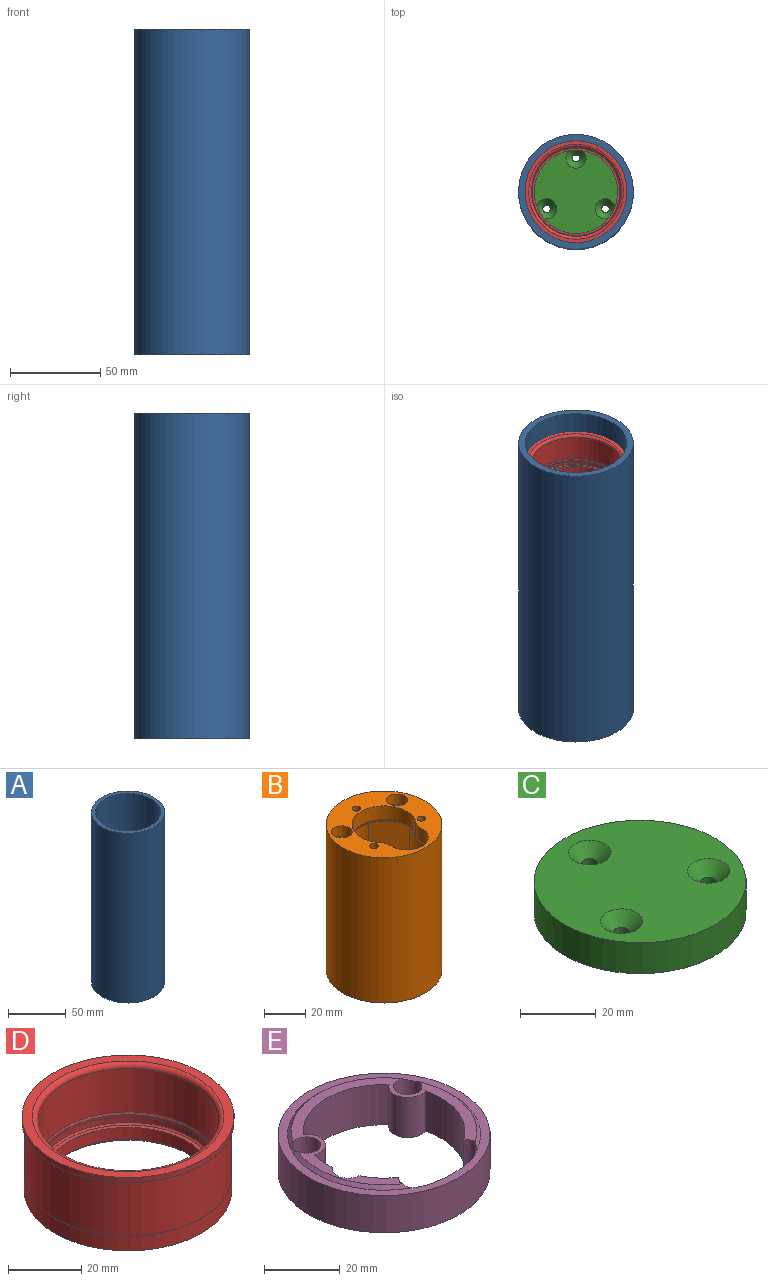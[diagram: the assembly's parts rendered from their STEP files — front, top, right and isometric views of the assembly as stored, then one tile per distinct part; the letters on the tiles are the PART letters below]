
ASSEMBLY  parts=5 mates=4
PART A: 8 faces, bbox 63.5x63.5x180 mm
  f0: cylinder r=31.75mm len=180mm, axis (0,0,-1), area 35908.4mm2, adj f2,f3
  f1: cylinder r=28.15mm len=167mm, axis (0,0,-1), area 29537.6mm2, adj f2,f5
  f2: plane 63.5x63.5mm, normal (0,0,1), area 677.5mm2, adj f0,f1
  f3: plane 63.5x63.5mm, normal (0,0,-1), area 433mm2, adj f0,f6
  f4: cylinder r=29mm len=58mm, axis (0,0,-1), area 2259.4mm2, adj f6,f7
  f5: plane 57.8x57.8mm, normal (0,0,-1), area 134.4mm2, adj f1,f7
  f6: cone r=29.5mm half-angle=45deg, axis (0,0,-1), area 130mm2, adj f3,f4
  f7: torus R=28.9mm, axis (0,0,1), area 28.6mm2, adj f4,f5
PART B: 43 faces, bbox 56x58.6x86 mm
  f0: plane 29.2x11.89mm, normal (0,0,-1), area 117.9mm2, adj f11,f19,f20,f21,f36,f38,f42
  f1: plane 30.94x12.61mm, normal (0,0,-1), area 119.4mm2, adj f4,f10,f16,f17,f29,f37,f38,f40
  f2: plane 8.18x5.6mm, normal (0,0,-1), area 12.5mm2, adj f13,f18,f19,f33
  f3: plane 8.18x5.6mm, normal (0,0,-1), area 12.5mm2, adj f13,f17,f18,f33
  f4: plane 75x8.69mm, normal (0.71,0.71,0), area 921.5mm2, adj f1,f5,f16,f29
  f5: plane 49x47.59mm, normal (0,0,-1), area 407.8mm2, adj f4,f6,f7,f15,f16,f17,f18,f19
  f6: cylinder r=2.65mm len=78mm, axis (0,0,1), area 1298.7mm2, adj f5,f28
  f7: cylinder r=2.65mm len=78mm, axis (0,0,1), area 1298.7mm2, adj f5,f26
  f8: cylinder r=28mm len=86mm, axis (0,0,1), area 15129.9mm2, adj f9,f23
  f9: plane 56x56mm, normal (0,0,1), area 1307.9mm2, adj f8,f10,f11,f13,f22,f25,f27,f32
  f10: cylinder r=2.1mm len=10mm, axis (0,0,1), area 131.8mm2, adj f1,f9,f37
  f11: cylinder r=2.1mm len=10mm, axis (0,0,1), area 131.9mm2, adj f0,f9,f36
  f12: cone r=0mm half-angle=59deg, axis (0,0,1), area 1.6mm2, adj f13,f18
  f13: cylinder r=2.1mm len=10mm, axis (0,0,1), area 131.9mm2, adj f2,f3,f9,f12,f33
  f14: cylinder r=9.75mm len=76.43mm, axis (0,0,-1), area 1167.3mm2, adj f15,f21,f23,f24,f38
  f15: plane 76.4x3.63mm, normal (0.71,0.71,0), area 383mm2, adj f5,f14,f24,f29,f38
  f16: cylinder r=9.75mm len=75mm, axis (0,0,-1), area 1148.6mm2, adj f1,f4,f5,f17
  f17: plane 75.03x14.03mm, normal (0.71,-0.71,0), area 1484.9mm2, adj f1,f3,f5,f16,f18,f35
  f18: cylinder r=9.75mm len=75mm, axis (0,0,-1), area 1148.6mm2, adj f2,f3,f5,f12,f17,f19
  f19: plane 75.03x14.03mm, normal (-0.71,-0.71,0), area 1484.9mm2, adj f0,f2,f5,f18,f20,f34
  f20: cylinder r=9.75mm len=75mm, axis (0,0,-1), area 1148.6mm2, adj f0,f5,f19,f21
  f21: plane 76.4x14.05mm, normal (-0.71,0.71,0), area 1487.8mm2, adj f0,f5,f14,f20,f24,f38
  f22: cylinder r=15.5mm len=31mm, axis (0,0,1), area 554.8mm2, adj f9,f33,f34,f35,f36,f37,f39,f41
  f23: plane 56x56mm, normal (0,0,-1), area 403.9mm2, adj f8,f14,f24
  f24: cone r=24.5mm half-angle=45deg, axis (0,0,-1), area 200.8mm2, adj f5,f14,f15,f21,f23
  f25: cylinder r=5mm len=10mm, axis (0,0,1), area 188.5mm2, adj f9,f30
  f26: plane 8x8mm, normal (0,0,1), area 28.2mm2, adj f7,f30
  f27: cylinder r=5mm len=10mm, axis (0,0,1), area 188.5mm2, adj f9,f31
  f28: plane 8x8mm, normal (0,0,1), area 28.2mm2, adj f6,f31
  f29: cylinder r=1.22mm len=75.14mm, axis (0,0,-1), area 287.9mm2, adj f1,f4,f5,f15,f38
  f30: torus R=4mm, axis (0,0,1), area 45.8mm2, adj f25,f26
  f31: torus R=4mm, axis (0,0,1), area 45.8mm2, adj f27,f28
  f32: cylinder r=10.5mm len=21mm, axis (0,0,-1), area 272.6mm2, adj f9,f38,f39,f41
  f33: torus R=17.5mm, axis (0,0,-1), area 58.4mm2, adj f2,f3,f13,f22,f34,f35
  f34: bspline ~7.3x7.25mm, area 18.2mm2, adj f19,f22,f33,f36
  f35: bspline ~7.3x7.25mm, area 18.2mm2, adj f17,f22,f33,f37
  f36: torus R=17.5mm, axis (0,0,-1), area 62.2mm2, adj f0,f11,f22,f34,f42
  f37: torus R=17.5mm, axis (0,0,-1), area 62.2mm2, adj f1,f10,f22,f35,f40
  f38: torus R=12.5mm, axis (0,0,-1), area 85.5mm2, adj f0,f1,f14,f15,f21,f29,f32,f40
  f39: cylinder r=8mm len=8mm, axis (0,0,-1), area 46mm2, adj f9,f22,f32,f40
  f40: torus R=6mm, axis (0,0,-1), area 16.4mm2, adj f1,f37,f38,f39
  f41: cylinder r=8mm len=8mm, axis (0,0,1), area 46mm2, adj f9,f22,f32,f42
  f42: torus R=6mm, axis (0,0,-1), area 16.4mm2, adj f0,f36,f38,f41
PART C: 9 faces, bbox 56x56x10 mm
  f0: cylinder r=28mm len=56mm, axis (0,0,1), area 1759.3mm2, adj f1,f2
  f1: plane 56x56mm, normal (0,0,-1), area 2421.4mm2, adj f0,f3,f5,f7
  f2: plane 56x56mm, normal (0,0,1), area 2167.4mm2, adj f0,f4,f6,f8
  f3: cylinder r=2.1mm len=6.5mm, axis (0,0,1), area 85.8mm2, adj f1,f4
  f4: cone r=2.1mm half-angle=45deg, axis (0,0,1), area 119.7mm2, adj f2,f3
  f5: cylinder r=2.1mm len=6.5mm, axis (0,0,1), area 85.8mm2, adj f1,f6
  f6: cone r=2.1mm half-angle=45deg, axis (0,0,1), area 119.7mm2, adj f2,f5
  f7: cylinder r=2.1mm len=6.5mm, axis (0,0,1), area 85.8mm2, adj f1,f8
  f8: cone r=2.1mm half-angle=45deg, axis (0,0,1), area 119.7mm2, adj f2,f7
PART D: 18 faces, bbox 61.7x61.7x25 mm
  f0: cylinder r=28.3mm len=56.6mm, axis (0,0,-1), area 3218.4mm2, adj f5,f17
  f1: cylinder r=24.7mm len=49.4mm, axis (0,0,-1), area 325.9mm2, adj f9,f13
  f2: plane 48.4x48.4mm, normal (0,0,1), area 170.7mm2, adj f3,f9
  f3: cylinder r=23.05mm len=46.1mm, axis (0,0,-1), area 579.3mm2, adj f2,f11
  f4: cylinder r=28.35mm len=56.7mm, axis (0,0,-1), area 890.6mm2, adj f5,f6
  f5: plane 56.7x56.7mm, normal (0,0,1), area 8.9mm2, adj f0,f4
  f6: plane 56.7x56.7mm, normal (0,0,-1), area 707.9mm2, adj f4,f11
  f7: cylinder r=24.7mm len=49.4mm, axis (0,0,-1), area 2246.6mm2, adj f10,f14
  f8: plane 58x58mm, normal (0,0,1), area 485.6mm2, adj f10,f15
  f9: cone r=24.2mm half-angle=45deg, axis (0,0,1), area 108.6mm2, adj f1,f2
  f10: torus R=26.2mm, axis (0,0,1), area 373.7mm2, adj f7,f8
  f11: cone r=24.05mm half-angle=45deg, axis (0,0,-1), area 209.3mm2, adj f3,f6
  f12: cylinder r=24.4mm len=48.8mm, axis (0,0,-1), area 107.3mm2, adj f13,f14
  f13: plane 49.4x49.4mm, normal (0,0,-1), area 46.3mm2, adj f1,f12
  f14: cone r=24.4mm half-angle=22.5deg, axis (0,0,1), area 120.9mm2, adj f7,f12
  f15: cylinder r=29mm len=58mm, axis (0,0,1), area 309.8mm2, adj f8,f16
  f16: plane 58x58mm, normal (0,0,-1), area 90.3mm2, adj f15,f17
  f17: torus R=28.5mm, axis (0,0,1), area 56mm2, adj f0,f16
PART E: 15 faces, bbox 56x56x13 mm
  f0: cylinder r=21.4mm len=13mm, axis (0,0,-1), area 96.4mm2, adj f1,f9,f12,f14
  f1: cylinder r=5mm len=13mm, axis (0,0,-1), area 189mm2, adj f0,f2,f12,f14
  f2: cylinder r=21.4mm len=32.11mm, axis (0,0,-1), area 472.1mm2, adj f1,f3,f12,f14
  f3: cylinder r=5mm len=13mm, axis (0,0,-1), area 189mm2, adj f2,f4,f12,f14
  f4: cylinder r=21.4mm len=22.99mm, axis (0,0,-1), area 339.6mm2, adj f3,f5,f12,f14
  f5: extruded ~26.96x13mm, area 450.7mm2, adj f4,f6,f11,f12,f13,f14
  f6: cylinder r=21.4mm len=13mm, axis (0,0,-1), area 137.9mm2, adj f5,f9,f12,f14
  f7: cylinder r=3.75mm len=13mm, axis (0,0,-1), area 304.2mm2, adj f12,f13,f14
  f8: cylinder r=28mm len=56mm, axis (0,0,-1), area 2111.2mm2, adj f11,f14
  f9: cylinder r=4.25mm len=13mm, axis (0,0,-1), area 137.4mm2, adj f0,f6,f12,f14
  f10: cylinder r=3.75mm len=13mm, axis (0,0,-1), area 304.2mm2, adj f12,f13,f14
  f11: plane 56x56mm, normal (0,0,1), area 417.2mm2, adj f5,f8,f13
  f12: plane 49x44.98mm, normal (0,0,1), area 336.3mm2, adj f0,f1,f2,f3,f4,f5,f6,f7
  f13: cone r=24.5mm half-angle=45deg, axis (0,0,-1), area 177.7mm2, adj f5,f7,f10,f11,f12
  f14: plane 56x56mm, normal (0,0,-1), area 879.2mm2, adj f0,f1,f2,f3,f4,f5,f6,f7
PLACE A rot(axis=(0,0,1),90deg) t=(-117.72,-12.63,-6)mm
PLACE B t=(-117.72,-12.63,115.29)mm
PLACE C t=(-117.72,-12.63,126.25)mm
PLACE D t=(-117.72,-12.63,136.79)mm
PLACE E t=(-117.72,-12.63,10.24)mm
MATE cylindrical C.f0 <-> B.f8  axis (0,0,-1) through (-117.72,-12.63,116.25)mm
MATE cylindrical E.f8 <-> A.f1  axis (0,0,-1) through (-117.72,-12.63,7.24)mm
MATE cylindrical B.f8 <-> E.f8  axis (0,0,-1) through (-117.72,-12.63,29.29)mm
MATE cylindrical A.f0 <-> D.f4  axis (0,0,-1) through (-117.72,-12.63,84)mm
